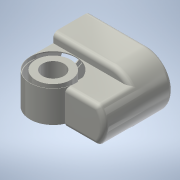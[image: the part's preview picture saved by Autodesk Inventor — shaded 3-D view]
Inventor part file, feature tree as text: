
AUTODESK INVENTOR PART (.ipt)
format: ipt  version: 2021 (Build 250183000, 183)  size: 353,280 bytes
history: native  units: mm (DEFAULTED — no unit token found)
features: extrude x13, sketch x12, fillet x3, hole x3, shell x1
ambient origin geometry x8: Origin, YZ Plane, XZ Plane, XY Plane, X Axis, Y Axis, Z Axis, Center Point
bodies: Solid1 (feature_tree)
feature tree (32):
  extrude  "押し出し1"  Depth=76.0mm TaperAngle=0.0deg
  extrude  "押し出し2"  Depth=2.0mm TaperAngle=0.0deg
  extrude  "押し出し3"  Depth=40.0mm
  extrude  "押し出し4"  Depth=20.0mm
  fillet  "Chamfer1"  Radius=180.0mm
  fillet  "Chamfer2"  Radius=116.0mm
  fillet  "Chamfer3"  Radius=90.0mm
  shell  "Shell1"  Thickness=74.0mm
  hole  "Hole1"  [1 undecoded]
  hole  "Hole2"  [1 undecoded]
  extrude  "Extrusion5"  Depth=2.0mm
  extrude  "Extrusion6"  Depth=10.0mm TaperAngle=0.0deg
  extrude  "Extrusion7"  Depth=10.0mm TaperAngle=0.0deg
  extrude  "Extrusion8"  Depth=10.0mm TaperAngle=0.0deg
  extrude  "Extrusion9"  Depth=58.0mm TaperAngle=0.0deg
  extrude  "Extrusion10"  Depth=69.0mm TaperAngle=0.0deg
  extrude  "Extrusion11"  Depth=69.0mm TaperAngle=0.0deg
  hole  "Hole3"  [1 undecoded]
  extrude  "Extrusion12"  [1 undecoded]
  extrude  "Extrusion13"  [1 undecoded]
  sketch  "Sketch5"  dims[d0=100.0mm d1=76.0mm d2=0.0mm]
  sketch  "Sketch6"  dims[d3=3.0mm d4=2.0mm d5=0.0mm]
  sketch  "Sketch7"  dims[d6=90.0mm d7=40.0mm]
  sketch  "Sketch8"  dims[d8=180.0mm d10=20.0mm d11=180.0mm d12=116.0mm d13=0.0mm d14=90.0mm d15=74.0mm]
  sketch  "Sketch9"  dims[d16=1.0mm d17=0.0mm d18=58.0mm]
  sketch  "Sketch10"  dims[d19=10.0mm d20=10.0mm]
  sketch  "Sketch11"  dims[d21=50.0mm d22=6.0mm d23=4.0mm d24=2.0mm d25=14.3117mm d26=2.0mm d27=20.594885mm d28=2.0mm]
  sketch  "Sketch12"  dims[d29=50.0mm d30=6.0mm d31=4.0mm d32=2.0mm d33=14.3117mm d34=2.0mm d35=20.594885mm d36=10.0mm d37=0.0mm]
  sketch  "Sketch13"  dims[d38=10.0mm d39=0.0mm d40=10.0mm d41=0.0mm]
  sketch  "Sketch14"  dims[d42=10.0mm d43=0.0mm d44=10.0mm d45=0.0mm]
  sketch  "Sketch15"  dims[d46=10.0mm d47=0.0mm d48=58.0mm d49=0.0mm]
  sketch  "Sketch16"  dims[d50=50.0mm d51=6.0mm d52=4.0mm d53=2.0mm d54=90.0deg d55=8.0mm d56=0.0mm d57=69.0mm d58=0.0mm d59=69.0mm d60=0.0mm]
note: 5 required parameter values undecoded (feature->parameter linkage not recoverable at this tier; creation-order binding heuristic only, values carry confidence <= 0.55)
